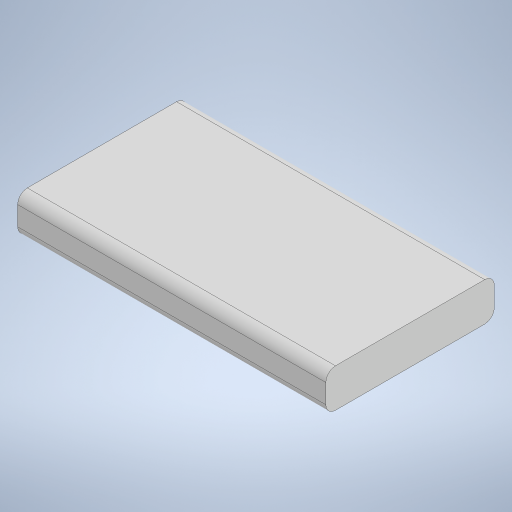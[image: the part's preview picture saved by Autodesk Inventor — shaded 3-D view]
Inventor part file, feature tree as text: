
AUTODESK INVENTOR PART (.ipt)
format: ipt  version: 2023 (Build 270158000, 158)  size: 209,920 bytes
history: native  units: mm
features: other x1, extrude x1, fillet x1, sketch x1
ambient origin geometry x8: Origin, YZ Plane, XZ Plane, XY Plane, X Axis, Y Axis, Z Axis, Center Point
bodies: Body1 (feature_tree)
feature tree (4):
  other  "Bryła1"
  extrude  "Wyciągnięcie proste1"  Depth=64.0mm
  fillet  "Zaokrąglenie1"  Radius=35.0mm
  sketch  "Szkic1"
